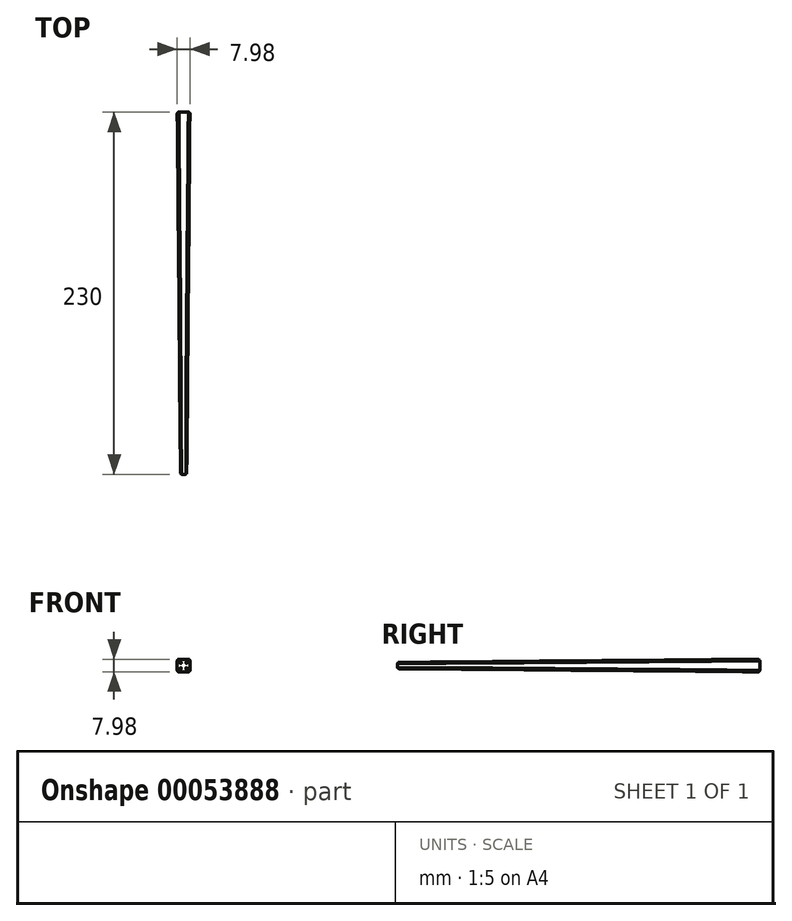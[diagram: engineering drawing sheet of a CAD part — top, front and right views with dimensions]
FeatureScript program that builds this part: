
annotation { "Feature Type Name" : "Feature", "Feature Type Description" : "" }
export const myFeature = defineFeature(function(context is Context, id is Id, definition is map)
    precondition{}
    {
        {
            var Q0;
            Q0=qCreatedBy(makeId("Front.planeOp"),FACE);
            var sketch = newSketch(context, id + "F0", { "sketchPlane" : qUnion([Q0])});
            skLineSegment(sketch, "E0.rect.bottom", {"start": v(4, 4) * mm, "end": v(-4, 4) * mm});
            skLineSegment(sketch, "E0.rect.top", {"start": v(4, -4) * mm, "end": v(-4, -4) * mm});
            skLineSegment(sketch, "E0.rect.left", {"start": v(4, 4) * mm, "end": v(4, -4) * mm});
            skLineSegment(sketch, "E0.rect.right", {"start": v(-4, 4) * mm, "end": v(-4, -4) * mm});
            skPoint(sketch, "E0.rect.middle", {"position": v(0, 0) * mm});
            skSolve(sketch);
        }
        {
            var Q0;
            Q0=qCreatedBy(makeId("Front.planeOp"),FACE);
            cPlane(context, id + "F1", {"entities" : qUnion([Q0]), "cplaneType" : CPlaneType.OFFSET, "offset" : 230 * mm, "width" : 150 * mm, "height" : 150 * mm});
        }
        {
            var Q0;
            Q0=qCreatedBy(id+"F1.planeOp",FACE);
            var sketch = newSketch(context, id + "F2", { "sketchPlane" : qUnion([Q0])});
            skLineSegment(sketch, "E1.0", {"start": v(4, -4) * mm, "end": v(-4, -4) * mm});
            skLineSegment(sketch, "E1.1", {"start": v(4, 4) * mm, "end": v(4, -4) * mm});
            skLineSegment(sketch, "E1.2", {"start": v(4, 4) * mm, "end": v(-4, 4) * mm});
            skLineSegment(sketch, "E1.3", {"start": v(-4, 4) * mm, "end": v(-4, -4) * mm});
            skPoint(sketch, "E1.4", {"position": v(0, 0) * mm});
            skCircle(sketch, "E2", {"center": v(0, 0) * mm, "radius": 2 * mm});
            skSolve(sketch);
        }
        {
            var Q0;
            Q0=makeQuery(id+"F0.imprint","IMPRINT",FACE,{"disambiguationData":[TD([[makeQuery(id+"F0.imprint","IMPRINT",EDGE,{"derivedFrom":sQuery(id+"F0.wireOp",EDGE,"E0.rect.bottom")}),1.0]])]});
            var Q1;
            Q1=makeQuery(id+"F2.imprint","IMPRINT",FACE,{"disambiguationData":[TD([[makeQuery(id+"F2.imprint","IMPRINT",EDGE,{"derivedFrom":sQuery(id+"F2.wireOp",EDGE,"E2")}),1.0]])]});
            loft(context, id + "F3", {"sheetProfilesArray" : [{ "sheetProfileEntities" : qUnion([Q0]) }, { "sheetProfileEntities" : qUnion([Q1]) }]});
        }
        {
            var Q0;
            Q0=makeQuery(id+"F3.opLoft","CAP_FACE",FACE,{"disambiguationData":[OSD([makeQuery(id+"F0.imprint","IMPRINT",FACE,{"disambiguationData":[TD([[makeQuery(id+"F0.imprint","IMPRINT",EDGE,{"derivedFrom":sQuery(id+"F0.wireOp",EDGE,"E0.rect.bottom")}),1.0]])]})])],"isStart":true});
            var Q1;
            Q1=makeQuery(id+"F3.opLoft","SWEPT_FACE",FACE,{"disambiguationData":[OSD([sQuery(id+"F0.wireOp",EDGE,"E0.rect.bottom"),sQuery(id+"F0.wireOp",EDGE,"E0.rect.left"),sQuery(id+"F0.wireOp",EDGE,"E0.rect.right"),sQuery(id+"F2.wireOp",EDGE,"E2")])]});
            var Q2;
            {var subQ0=sQuery(id+"F2.wireOp",EDGE,"E2");var subQ1=sQuery(id+"F0.wireOp",EDGE,"E0.rect.left");var subQ2=sQuery(id+"F0.wireOp",EDGE,"E0.rect.right");var subQ3=sQuery(id+"F0.wireOp",EDGE,"E0.rect.top");var subQ4=sQuery(id+"F0.wireOp",EDGE,"E0.rect.bottom");Q2=makeQuery(id+"F3.opLoft","SWEPT_FACE",FACE,{"disambiguationData":[OSD([subQ4,subQ3,subQ1,subQ2,subQ0]),TDD([makeQuery(id+"F0.imprint","INTERSECT",VERTEX,{"derivedFrom":[subQ4,subQ1]}),makeQuery(id+"F0.imprint","INTERSECT",VERTEX,{"derivedFrom":[subQ3,subQ1]}),makeQuery(id+"F0.imprint","INTERSECT",VERTEX,{"derivedFrom":[subQ3,subQ2]}),makeQuery(id+"F0.imprint","IMPRINT",EDGE,{"derivedFrom":subQ1}),makeQuery(id+"F2.imprint","IMPRINT",EDGE,{"derivedFrom":subQ0})])]});}
            var Q3;
            {var subQ0=sQuery(id+"F2.wireOp",EDGE,"E2");var subQ1=sQuery(id+"F0.wireOp",EDGE,"E0.rect.right");var subQ2=sQuery(id+"F0.wireOp",EDGE,"E0.rect.top");var subQ3=sQuery(id+"F0.wireOp",EDGE,"E0.rect.bottom");var subQ4=sQuery(id+"F0.wireOp",EDGE,"E0.rect.left");Q3=makeQuery(id+"F3.opLoft","SWEPT_FACE",FACE,{"disambiguationData":[OSD([subQ3,subQ2,subQ4,subQ1,subQ0]),TDD([makeQuery(id+"F0.imprint","INTERSECT",VERTEX,{"derivedFrom":[subQ3,subQ4]}),makeQuery(id+"F0.imprint","INTERSECT",VERTEX,{"derivedFrom":[subQ3,subQ1]}),makeQuery(id+"F0.imprint","INTERSECT",VERTEX,{"derivedFrom":[subQ2,subQ1]}),makeQuery(id+"F0.imprint","IMPRINT",EDGE,{"derivedFrom":subQ1}),makeQuery(id+"F2.imprint","IMPRINT",EDGE,{"derivedFrom":subQ0})])]});}
            var Q4;
            {var subQ0=sQuery(id+"F2.wireOp",EDGE,"E2");var subQ1=sQuery(id+"F0.wireOp",EDGE,"E0.rect.top");var subQ2=sQuery(id+"F0.wireOp",EDGE,"E0.rect.right");var subQ3=sQuery(id+"F0.wireOp",EDGE,"E0.rect.left");var subQ4=sQuery(id+"F0.wireOp",EDGE,"E0.rect.bottom");Q4=makeQuery(id+"F3.opLoft","SWEPT_FACE",FACE,{"disambiguationData":[OSD([subQ4,subQ1,subQ3,subQ2,subQ0]),TDD([makeQuery(id+"F0.imprint","INTERSECT",VERTEX,{"derivedFrom":[subQ4,subQ2]}),makeQuery(id+"F0.imprint","INTERSECT",VERTEX,{"derivedFrom":[subQ1,subQ3]}),makeQuery(id+"F0.imprint","INTERSECT",VERTEX,{"derivedFrom":[subQ1,subQ2]}),makeQuery(id+"F0.imprint","IMPRINT",EDGE,{"derivedFrom":subQ1}),makeQuery(id+"F2.imprint","IMPRINT",EDGE,{"derivedFrom":subQ0})])]});}
            fillet(context, id + "F4", {"entities" : qUnion([Q0, Q1, Q2, Q3, Q4]), "radius" : .95 * mm, "tangentPropagation" : true, "allowEdgeOverflow" : false});
        }
    });
